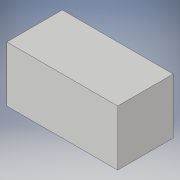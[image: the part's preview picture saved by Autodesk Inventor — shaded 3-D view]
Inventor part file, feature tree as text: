
AUTODESK INVENTOR PART (.ipt)
format: ipt  version: 2018 (Build 220112000, 112)  size: 86,016 bytes
history: native  units: mm
features: extrude x1, sketch x1
ambient origin geometry x8: Origin, YZ Plane, XZ Plane, XY Plane, X Axis, Y Axis, Z Axis, Center Point
bodies: Volumenkörper1 (feature_tree)
feature tree (2):
  extrude  "Extrusion1"  Depth=30.0mm
  sketch  "Skizze1"  dims[d0=15.0mm d1=30.0mm d2=30.0mm d3=60.0mm d4=30.0mm d5=0.0mm]
